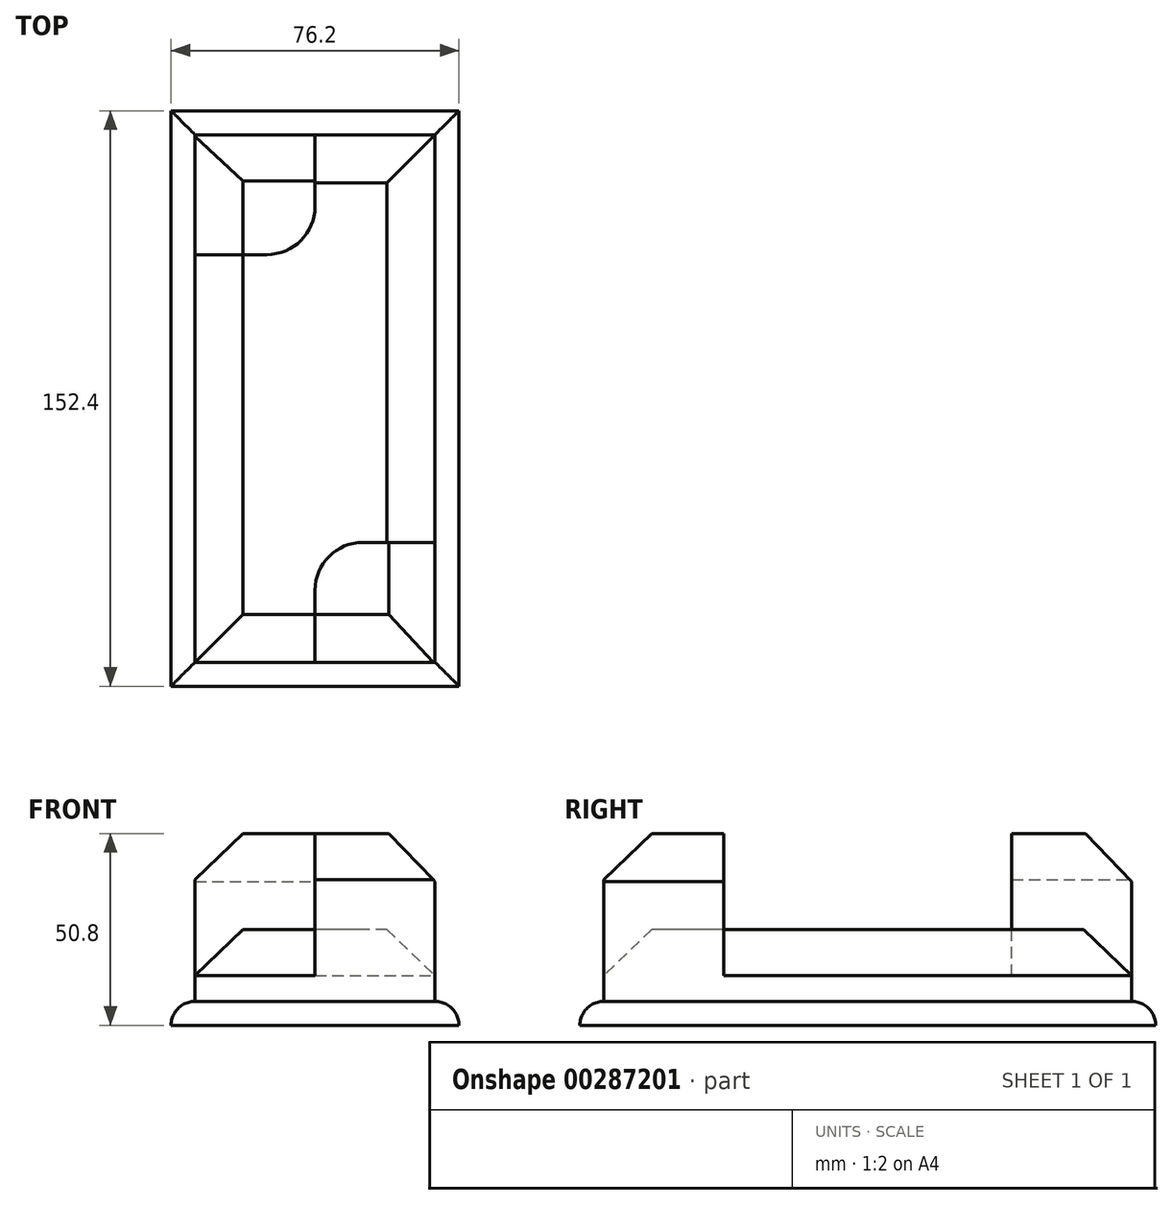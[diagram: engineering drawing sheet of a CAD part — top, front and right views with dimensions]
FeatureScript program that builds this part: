
annotation { "Feature Type Name" : "Feature", "Feature Type Description" : "" }
export const myFeature = defineFeature(function(context is Context, id is Id, definition is map)
    precondition{}
    {
        {
            var Q0;
            Q0=qCreatedBy(makeId("Top.planeOp"),FACE);
            var sketch = newSketch(context, id + "F0", { "sketchPlane" : qUnion([Q0])});
            skLineSegment(sketch, "E0.bottom", {"start": v(-38.1, 6.35) * mm, "end": v(38.1, 6.35) * mm});
            skLineSegment(sketch, "E0.top", {"start": v(-38.1, -146.05) * mm, "end": v(38.1, -146.05) * mm});
            skLineSegment(sketch, "E0.left", {"start": v(-38.1, 6.35) * mm, "end": v(-38.1, -146.05) * mm});
            skLineSegment(sketch, "E0.right", {"start": v(38.1, 6.35) * mm, "end": v(38.1, -146.05) * mm});
            skLineSegment(sketch, "E1.bottom", {"start": v(-31.75, 0) * mm, "end": v(31.75, 0) * mm});
            skLineSegment(sketch, "E1.top", {"start": v(-31.75, -139.7) * mm, "end": v(31.75, -139.7) * mm});
            skLineSegment(sketch, "E1.left", {"start": v(-31.75, 0) * mm, "end": v(-31.75, -139.7) * mm});
            skLineSegment(sketch, "E1.right", {"start": v(31.75, 0) * mm, "end": v(31.75, -139.7) * mm});
            skLineSegment(sketch, "E2", {"start": v(-31.75, -31.75) * mm, "end": v(-12.7, -31.75) * mm});
            skLineSegment(sketch, "E3", {"start": v(0, -19.05) * mm, "end": v(0, 0) * mm});
            skLineSegment(sketch, "E4", {"start": v(31.75, -107.95) * mm, "end": v(12.7, -107.95) * mm});
            skLineSegment(sketch, "E5", {"start": v(0, -120.65) * mm, "end": v(0, -139.7) * mm});
            skPoint(sketch, "E6.visualSharp", {"position": v(0, -31.75) * mm});
            skArc(sketch, "E6.filletArc", {"start": v(-12.7, -31.75) * mm, "mid": v(-3.72, -28.03) * mm, "end": v(0, -19.05) * mm});
            skPoint(sketch, "E7.visualSharp", {"position": v(0, -107.95) * mm});
            skArc(sketch, "E7.filletArc", {"start": v(12.7, -107.95) * mm, "mid": v(3.72, -111.67) * mm, "end": v(0, -120.65) * mm});
            skSolve(sketch);
        }
        {
            var Q0;
            Q0 = qSketchRegion(id + "F0", true);
            extrude(context, id + "F1", {"entities" : qUnion([Q0]), "depth" : 6.35 * mm});
        }
        {
            var Q0;
            {var subQ3=sQuery(id+"F0.wireOp",EDGE,"E2");Q0=makeQuery(id+"F0.imprint","IMPRINT",FACE,{"disambiguationData":[TD([[makeQuery(id+"F0.imprint","IMPRINT",EDGE,{"derivedFrom":subQ3}),-1.0]])]});}
            extrude(context, id + "F2", {"entities" : qUnion([Q0]), "operationType" : NewBodyOperationType.ADD, "depth" : 25.4 * mm});
        }
        {
            var Q0;
            {var subQ0=sQuery(id+"F0.wireOp",EDGE,"E2");Q0=makeQuery(id+"F0.imprint","IMPRINT",FACE,{"disambiguationData":[TD([[makeQuery(id+"F0.imprint","IMPRINT",EDGE,{"derivedFrom":subQ0}),1.0]])]});}
            var Q1;
            {var subQ1=sQuery(id+"F0.wireOp",EDGE,"E4");Q1=makeQuery(id+"F0.imprint","IMPRINT",FACE,{"disambiguationData":[TD([[makeQuery(id+"F0.imprint","IMPRINT",EDGE,{"derivedFrom":subQ1}),1.0]])]});}
            extrude(context, id + "F3", {"entities" : qUnion([Q0, Q1]), "operationType" : NewBodyOperationType.ADD, "depth" : 50.8 * mm});
        }
        {
            var Q0;
            Q0=makeQuery(id+"F2.opExtrude","CAP_EDGE",EDGE,{"disambiguationData":[OSD([sQuery(id+"F0.wireOp",EDGE,"E1.left")])],"isStart":false});
            var Q1;
            Q1=makeQuery(id+"F2.opExtrude","CAP_EDGE",EDGE,{"disambiguationData":[OSD([sQuery(id+"F0.wireOp",EDGE,"E1.top")])],"isStart":false});
            var Q2;
            Q2=makeQuery(id+"F2.opExtrude","CAP_EDGE",EDGE,{"disambiguationData":[OSD([sQuery(id+"F0.wireOp",EDGE,"E1.right")])],"isStart":false});
            var Q3;
            Q3=makeQuery(id+"F3.opExtrude","CAP_EDGE",EDGE,{"disambiguationData":[OSD([sQuery(id+"F0.wireOp",EDGE,"E1.right")])],"isStart":false});
            var Q4;
            Q4=makeQuery(id+"F3.opExtrude","CAP_EDGE",EDGE,{"disambiguationData":[OSD([sQuery(id+"F0.wireOp",EDGE,"E1.top")])],"isStart":false});
            var Q5;
            Q5=makeQuery(id+"F3.opExtrude","CAP_EDGE",EDGE,{"disambiguationData":[OSD([sQuery(id+"F0.wireOp",EDGE,"E1.bottom")])],"isStart":false});
            var Q6;
            Q6=makeQuery(id+"F3.opExtrude","CAP_EDGE",EDGE,{"disambiguationData":[OSD([sQuery(id+"F0.wireOp",EDGE,"E1.left")])],"isStart":false});
            var Q7;
            Q7=makeQuery(id+"F2.opExtrude","CAP_EDGE",EDGE,{"disambiguationData":[OSD([sQuery(id+"F0.wireOp",EDGE,"E1.bottom")])],"isStart":false});
            chamfer(context, id + "F4", {"entities" : qUnion([Q0, Q1, Q2, Q3, Q4, Q5, Q6, Q7]), "chamferType" : ChamferType.OFFSET_ANGLE, "width" : 12.7 * mm, "oppositeDirection" : false, "angle" : 44 * degree, "tangentPropagation" : true});
        }
        {
            var Q0;
            Q0=makeQuery(id+"F1.opExtrude","CAP_EDGE",EDGE,{"disambiguationData":[OSD([sQuery(id+"F0.wireOp",EDGE,"E0.right")])],"isStart":false});
            var Q1;
            Q1=makeQuery(id+"F1.opExtrude","CAP_EDGE",EDGE,{"disambiguationData":[OSD([sQuery(id+"F0.wireOp",EDGE,"E0.bottom")])],"isStart":false});
            var Q2;
            Q2=makeQuery(id+"F1.opExtrude","CAP_EDGE",EDGE,{"disambiguationData":[OSD([sQuery(id+"F0.wireOp",EDGE,"E0.left")])],"isStart":false});
            var Q3;
            Q3=makeQuery(id+"F1.opExtrude","CAP_EDGE",EDGE,{"disambiguationData":[OSD([sQuery(id+"F0.wireOp",EDGE,"E0.top")])],"isStart":false});
            fillet(context, id + "F5", {"entities" : qUnion([Q0, Q1, Q2, Q3]), "radius" : 6.35 * mm, "tangentPropagation" : true, "allowEdgeOverflow" : false});
        }
    });
